# Revit family: Lighting_Fixture-Wall-Astro-Toscaxxx
name_source: partatom
category: Lighting Fixtures
revit_build: Autodesk Revit LT 2014 (Build: 20130308_1515(x64)
units: mm (PartAtom-declared; Revit-internal decimal feet)

## types (3) — shared parameters
Apparent Load = 2 VA
Arm Length = 159.25 mm  [stored 0.522474 ft]
Assembly Code = D5020200
Class = 1
Description = Wall Light
Dimmable = No
Height = 45 mm  [stored 0.147638 ft]
IP Rating = IP20
Lamp = LED
Lamp included = Yes
Length = 42.75 mm  [stored 0.140256 ft]
Lens Material = Astro - Glass - Clear
Luminaire Lamp Efficiency Rating = A
Manufacturer = Astro Lighting Ltd, CM20 2DP
Mountable on normally flammable surfaces = Yes
Number of Poles = 1
Product Documentation = http://www.astrolighting.co.uk
Suitable for bathroom zone = Zone 3
Type Comments = Includes integral LED driver. Includes integral switch.
URL = www.astrolighting.co.uk
Voltage = 230 V
Wattage Comments = 1w
Weight = 1.2kg
Width = 200 mm  [stored 0.656168 ft]

## per-type parameters (varying)
| type | Casing Material | Model |
| 0699 Tosca (Matt Nickel) | Astro - Steel - Matt Nickel | 0699 Tosca Matt Nickel |
| 0849 Tosca (Bronze) | Astro - Steel - Bronze | 0849 Tosca Bronze |
| 0850 Tosca (Chrome) | Astro - Steel - Chrome Finish | 0850 Tosca Chrome |

note: [stored X ft] marks values corroborated as IEEE doubles in the binary element streams (Revit-internal decimal feet)

## geometry (parser evidence)
native form markers: Sweep x5
no freeform markers — native parametric forms only
